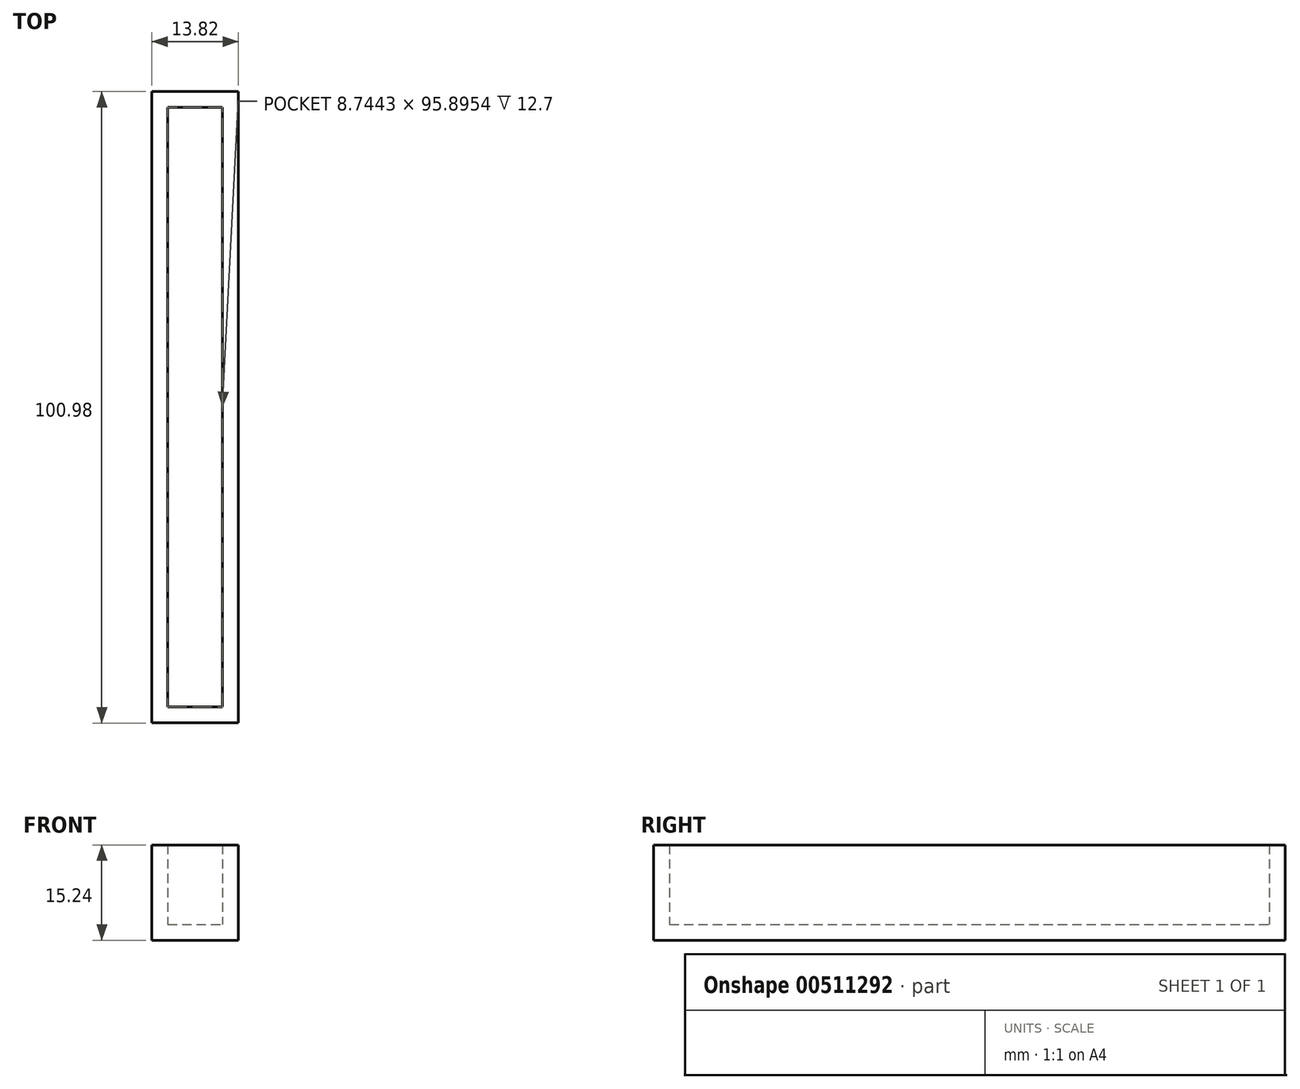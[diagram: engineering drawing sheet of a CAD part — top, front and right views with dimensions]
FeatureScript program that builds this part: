
annotation { "Feature Type Name" : "Feature", "Feature Type Description" : "" }
export const myFeature = defineFeature(function(context is Context, id is Id, definition is map)
    precondition{}
    {
        {
            var Q0;
            Q0=qCreatedBy(makeId("Top.planeOp"),FACE);
            var sketch = newSketch(context, id + "F0", { "sketchPlane" : qUnion([Q0])});
            skLineSegment(sketch, "E0.bottom", {"start": v(27.1, -61.36) * mm, "end": v(35.85, -61.36) * mm});
            skLineSegment(sketch, "E0.top", {"start": v(27.1, 34.54) * mm, "end": v(35.85, 34.54) * mm});
            skLineSegment(sketch, "E0.left", {"start": v(27.1, -61.36) * mm, "end": v(27.1, 34.54) * mm});
            skLineSegment(sketch, "E0.right", {"start": v(35.85, -61.36) * mm, "end": v(35.85, 34.54) * mm});
            skSolve(sketch);
        }
        {
            var Q0;
            Q0=makeQuery(id+"F0.imprint","IMPRINT",FACE,{"disambiguationData":[TD([[makeQuery(id+"F0.imprint","IMPRINT",EDGE,{"derivedFrom":sQuery(id+"F0.wireOp",EDGE,"E0.bottom")}),1.0]])]});
            extrude(context, id + "F1", {"entities" : qUnion([Q0]), "depth" : 12.7 * mm});
        }
        {
            var Q0;
            Q0=qCreatedBy(makeId("Top.planeOp"),FACE);
            var sketch = newSketch(context, id + "F2", { "sketchPlane" : qUnion([Q0])});
            skArc(sketch, "E1", {"start": v(36.58, -60.63) * mm, "mid": v(74.55, -12.76) * mm, "end": v(35.7, 34.4) * mm});
            skSolve(sketch);
        }
        {
            var Q0;
            Q0=sQuery(id+"F2.wireOp",EDGE,"E1");
            extrude(context, id + "F3", {"bodyType" : ToolBodyType.SURFACE, "surfaceEntities" : qUnion([Q0]), "depth" : 12.7 * mm});
        }
        {
            var Q0;
            Q0=makeQuery(id+"F1.opExtrude","CAP_FACE",FACE,{"disambiguationData":[OSD([sQuery(id+"F0.wireOp",EDGE,"E0.bottom"),sQuery(id+"F0.wireOp",EDGE,"E0.top"),sQuery(id+"F0.wireOp",EDGE,"E0.left"),sQuery(id+"F0.wireOp",EDGE,"E0.right")])],"isStart":false});
            var Q1;
            Q1=makeQuery(id+"F1.opExtrude","SWEPT_BODY",BODY,{"disambiguationData":[OSD([sQuery(id+"F0.wireOp",EDGE,"E0.bottom"),sQuery(id+"F0.wireOp",EDGE,"E0.top"),sQuery(id+"F0.wireOp",EDGE,"E0.left"),sQuery(id+"F0.wireOp",EDGE,"E0.right")])]});
            shell(context, id + "F4", {"entities" : qUnion([Q0]), "parts" : qUnion([Q1]), "thickness" : 2.54 * mm, "oppositeDirection" : true});
        }
    });
